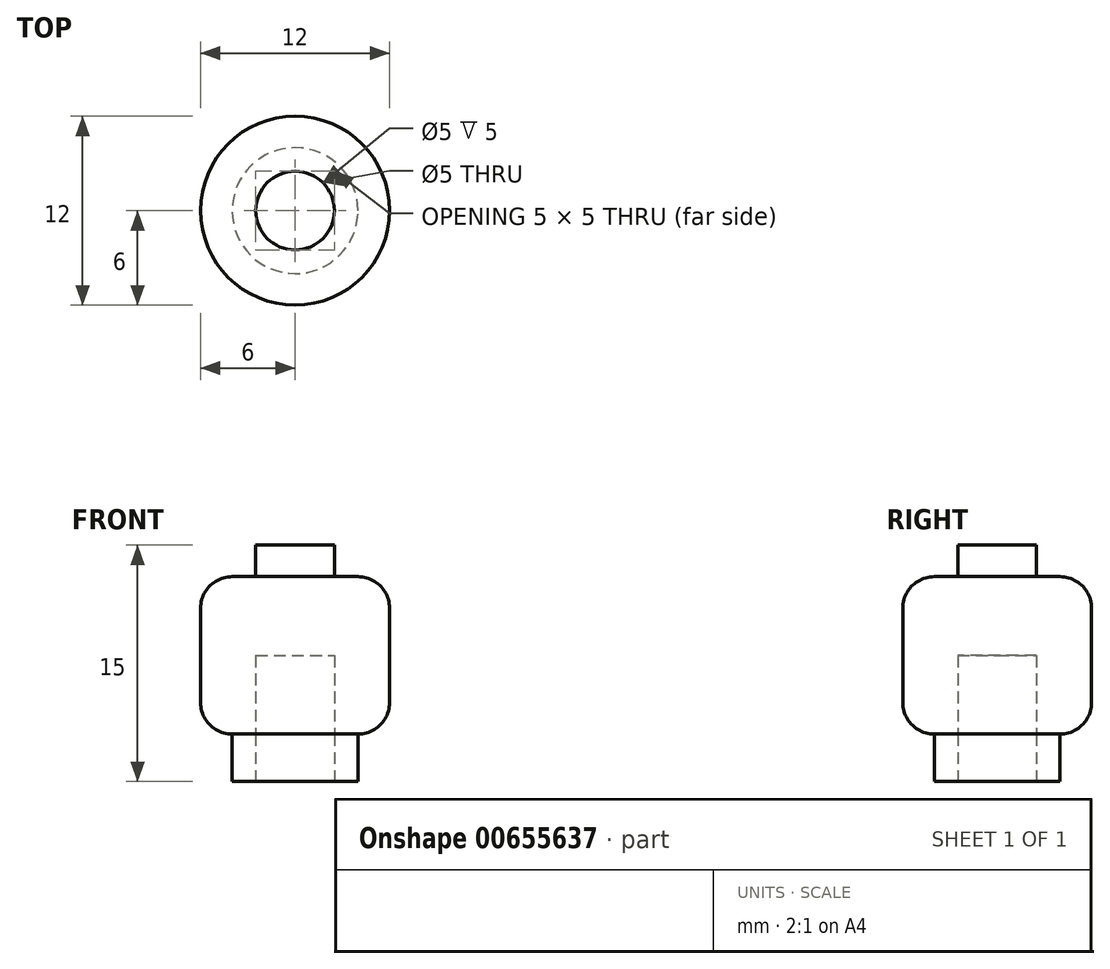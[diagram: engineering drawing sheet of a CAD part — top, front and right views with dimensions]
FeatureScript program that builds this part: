
annotation { "Feature Type Name" : "Feature", "Feature Type Description" : "" }
export const myFeature = defineFeature(function(context is Context, id is Id, definition is map)
    precondition{}
    {
        {
            var Q0;
            Q0=qCreatedBy(makeId("Top.planeOp"),FACE);
            var sketch = newSketch(context, id + "F0", { "sketchPlane" : qUnion([Q0])});
            skCircle(sketch, "E0", {"center": v(0, 0) * mm, "radius": 4 * mm});
            skSolve(sketch);
        }
        {
            var Q0;
            Q0 = qSketchRegion(id + "F0", true);
            extrude(context, id + "F1", {"entities" : qUnion([Q0]), "depth" : 3 * mm, "offsetDistance" : 25 * mm});
        }
        {
            var Q0;
            Q0=makeQuery(id+"F1.opExtrude","CAP_FACE",FACE,{"disambiguationData":[OSD([sQuery(id+"F0.wireOp",EDGE,"E0")])],"isStart":false});
            var sketch = newSketch(context, id + "F2", { "sketchPlane" : qUnion([Q0])});
            skCircle(sketch, "E1", {"center": v(0, 0) * mm, "radius": 6 * mm});
            skSolve(sketch);
        }
        {
            var Q0;
            Q0 = qSketchRegion(id + "F2", true);
            extrude(context, id + "F3", {"entities" : qUnion([Q0]), "depth" : 10 * mm, "offsetDistance" : 25 * mm});
        }
        {
            var Q0;
            Q0=makeQuery(id+"F3.opExtrude","CAP_FACE",FACE,{"disambiguationData":[OSD([sQuery(id+"F2.wireOp",EDGE,"E1")])],"isStart":false});
            var sketch = newSketch(context, id + "F4", { "sketchPlane" : qUnion([Q0])});
            skCircle(sketch, "E2", {"center": v(0, 0) * mm, "radius": 2.5 * mm});
            skSolve(sketch);
        }
        {
            var Q0;
            Q0 = qSketchRegion(id + "F4", true);
            extrude(context, id + "F5", {"entities" : qUnion([Q0]), "operationType" : NewBodyOperationType.ADD, "depth" : 2 * mm, "offsetDistance" : 25 * mm});
        }
        {
            var Q0;
            Q0=makeQuery(id+"F3.opExtrude","CAP_EDGE",EDGE,{"disambiguationData":[OSD([sQuery(id+"F2.wireOp",EDGE,"E1")])],"isStart":false});
            var Q1;
            Q1=makeQuery(id+"F3.opExtrude","CAP_EDGE",EDGE,{"disambiguationData":[OSD([sQuery(id+"F2.wireOp",EDGE,"E1")])],"isStart":true});
            fillet(context, id + "F6", {"entities" : qUnion([Q0, Q1]), "radius" : 2 * mm, "tangentPropagation" : true, "allowEdgeOverflow" : false});
        }
        {
            var Q0;
            Q0=makeQuery(id+"F1.opExtrude","CAP_FACE",FACE,{"disambiguationData":[OSD([sQuery(id+"F0.wireOp",EDGE,"E0")])],"isStart":true});
            var sketch = newSketch(context, id + "F7", { "sketchPlane" : qUnion([Q0])});
            skCircle(sketch, "E3", {"center": v(0, 0) * mm, "radius": 2.5 * mm});
            skSolve(sketch);
        }
        {
            var Q0;
            Q0 = qSketchRegion(id + "F7", true);
            extrude(context, id + "F8", {"entities" : qUnion([Q0]), "operationType" : NewBodyOperationType.REMOVE, "oppositeDirection" : true, "depth" : 8 * mm, "offsetDistance" : 25 * mm});
        }
    });
